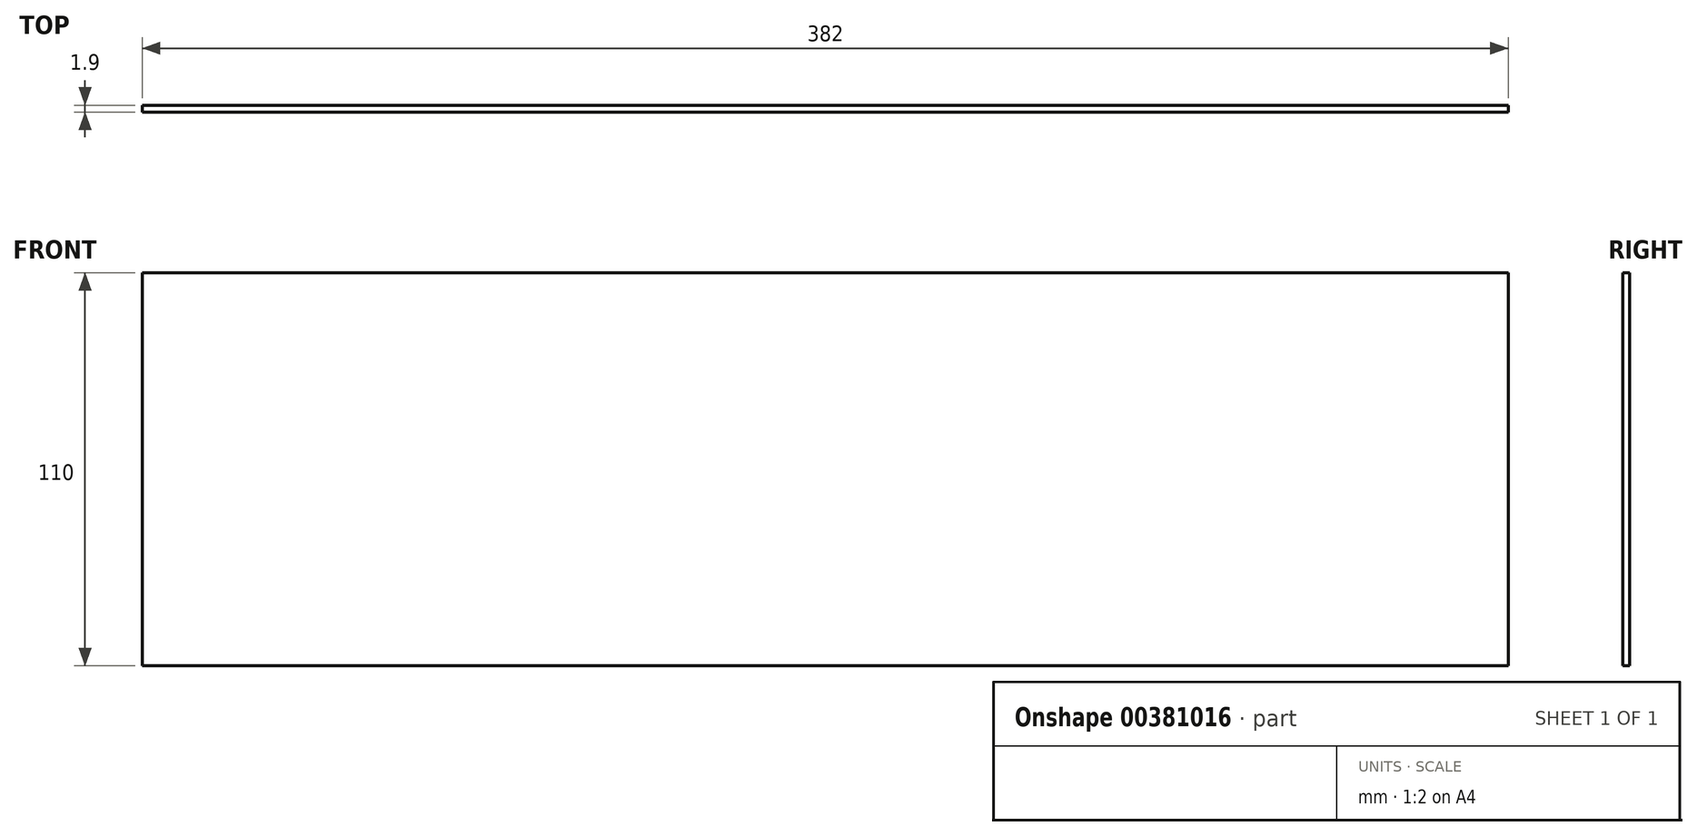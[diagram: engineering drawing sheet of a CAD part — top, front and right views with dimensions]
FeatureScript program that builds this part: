
annotation { "Feature Type Name" : "Feature", "Feature Type Description" : "" }
export const myFeature = defineFeature(function(context is Context, id is Id, definition is map)
    precondition{}
    {
        {
            var Q0;
            Q0=qCreatedBy(makeId("Front.planeOp"),FACE);
            var sketch = newSketch(context, id + "F0", { "sketchPlane" : qUnion([Q0])});
            skLineSegment(sketch, "E0.bottom", {"start": v(-191, 55) * mm, "end": v(191, 55) * mm});
            skLineSegment(sketch, "E0.top", {"start": v(-191, -55) * mm, "end": v(191, -55) * mm});
            skLineSegment(sketch, "E0.left", {"start": v(-191, 55) * mm, "end": v(-191, -55) * mm});
            skLineSegment(sketch, "E0.right", {"start": v(191, 55) * mm, "end": v(191, -55) * mm});
            skPoint(sketch, "E0.middle", {"position": v(0, 0) * mm});
            skSolve(sketch);
        }
        {
            var Q0;
            Q0=makeQuery(id+"F0.imprint","IMPRINT",FACE,{"disambiguationData":[TD([[makeQuery(id+"F0.imprint","IMPRINT",EDGE,{"derivedFrom":sQuery(id+"F0.wireOp",EDGE,"E0.bottom")}),-1.0]])]});
            extrude(context, id + "F1", {"entities" : qUnion([Q0]), "depth" : 1.9 * mm});
        }
    });
